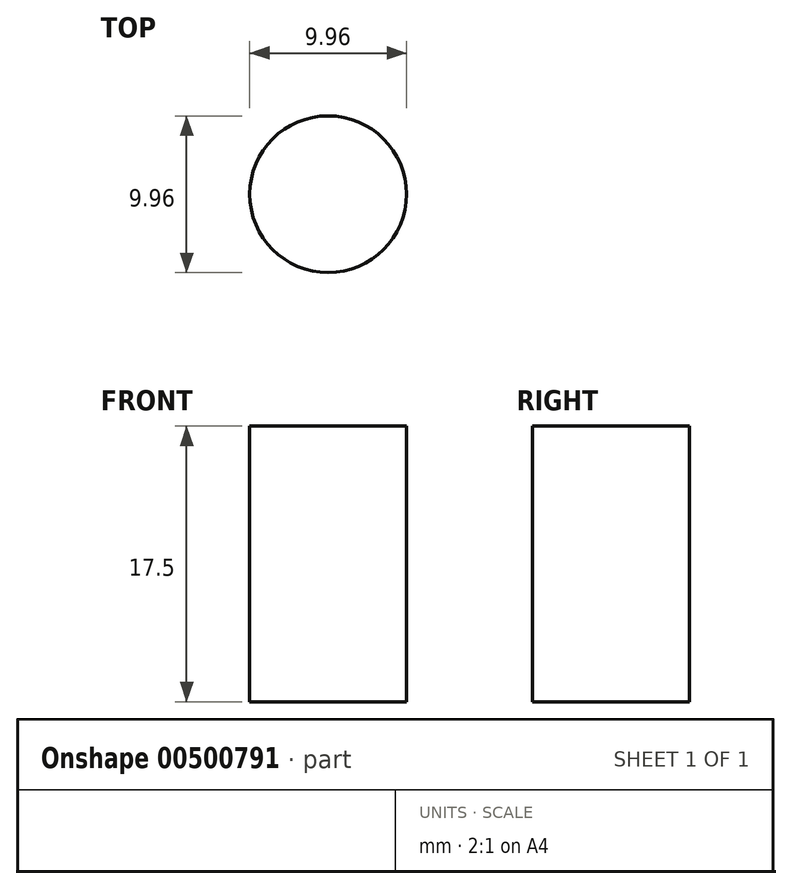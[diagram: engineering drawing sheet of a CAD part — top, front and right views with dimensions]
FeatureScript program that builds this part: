
annotation { "Feature Type Name" : "Feature", "Feature Type Description" : "" }
export const myFeature = defineFeature(function(context is Context, id is Id, definition is map)
    precondition{}
    {
        {
            var Q0;
            Q0=qCreatedBy(makeId("Top.planeOp"),FACE);
            var sketch = newSketch(context, id + "F0", { "sketchPlane" : qUnion([Q0])});
            skCircle(sketch, "E0", {"center": v(0, 0) * mm, "radius": 4.97 * mm});
            skSolve(sketch);
        }
        {
            var Q0;
            Q0 = qSketchRegion(id + "F0", true);
            extrude(context, id + "F1", {"entities" : qUnion([Q0]), "depth" : 17.5 * mm, "offsetDistance" : 25 * mm});
        }
    });
